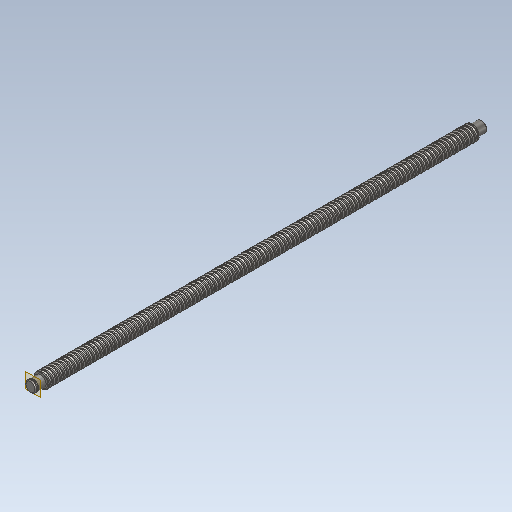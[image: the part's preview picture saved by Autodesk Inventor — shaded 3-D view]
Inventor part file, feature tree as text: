
AUTODESK INVENTOR PART (.ipt)
format: ipt  version: 2020 (Build 240168000, 168)  size: 878,592 bytes
history: native  units: mm
features: sketch x7, extrude x6, other x3, chamfer x2
ambient origin geometry x8: Origin, YZ Plane, XZ Plane, XY Plane, X Axis, Y Axis, Z Axis, Center Point
bodies: Body1 (feature_tree)
feature tree (18):
  other  "Bryła1"
  extrude  "Wyciągnięcie proste1"  Depth=13.64mm
  other  "Zwój1"
  extrude  "Wyciągnięcie proste2"  Depth=487.5mm TaperAngle=0.0deg
  extrude  "Wyciągnięcie proste3"  TaperAngle=120.0deg  [1 undecoded]
  extrude  "Wyciągnięcie proste4"  TaperAngle=120.0deg  [1 undecoded]
  other  "Płaszczyzna konstrukcyjna1"
  extrude  "Wyciągnięcie proste5"  Depth=8.0mm
  chamfer  "Faza1"  Distance=1.0mm
  extrude  "Wyciągnięcie proste6"  Depth=20.0mm
  chamfer  "Faza2"  Distance=12.0mm
  sketch  "Szkic1"
  sketch  "Szkic2"
  sketch  "Szkic3"
  sketch  "Szkic4"
  sketch  "Szkic5"
  sketch  "Szkic7"
  sketch  "Szkic8"
note: 2 required parameter values undecoded (feature->parameter linkage not recoverable at this tier; creation-order binding heuristic only, values carry confidence <= 0.55)
